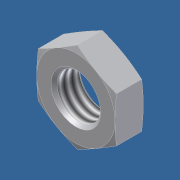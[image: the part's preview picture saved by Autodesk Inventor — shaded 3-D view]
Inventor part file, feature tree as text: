
AUTODESK INVENTOR PART (.ipt)
format: ipt  version: unknown  size: 220,160 bytes
history: native  units: in
note: dims shown in document units (in); Inventor stores cm internally (conversion verified against a paired STEP export)
features: other x70, sketch x3, revolve x2, extrude x1, thread x1
ambient origin geometry x8: Origin, YZ Plane, XZ Plane, XY Plane, X Axis, Y Axis, Z Axis, Center Point
feature tree (77):
  sketch  "Sketch_8"  dims[d0=360.0deg d1=0.25in d2=0.0in]
  sketch  "Sketch_10"  dims[d3=360.0deg d4=0.25in d5=0.0in]
  revolve  "Revolution1"  [1 undecoded]
  extrude  "Extrusion1"  Depth=0.25in TaperAngle=0.0deg
  revolve  "Revolution2"  [1 undecoded]
  thread  "Thread1"  [1 undecoded]
  other  "NUT_XY"
  other  "NUT_YZ"
  other  "NUT_ZX"
  other  "NUT_X"
  other  "NUT_Y"
  other  "NUT_Z"
  other  "NUT_Center"
  other  "a1_XY"
  other  "a1_YZ"
  other  "a1_ZX"
  other  "a1_X"
  other  "a1_Y"
  other  "a1_Z"
  other  "a1_Center"
  other  "a2_XY"
  other  "a2_YZ"
  other  "a2_ZX"
  other  "a2_X"
  other  "a2_Y"
  other  "a2_Z"
  other  "a2_Center"
  other  "b1_XY"
  other  "b1_YZ"
  other  "b1_ZX"
  other  "b1_X"
  other  "b1_Y"
  other  "b1_Z"
  other  "b1_Center"
  other  "b2_XY"
  other  "b2_YZ"
  other  "b2_ZX"
  other  "b2_X"
  other  "b2_Y"
  other  "b2_Z"
  other  "b2_Center"
  other  "e_XY"
  other  "e_YZ"
  other  "e_ZX"
  other  "e_X"
  other  "e_Y"
  other  "e_Z"
  other  "e_Center"
  other  "ol1_XY"
  other  "ol1_YZ"
  other  "ol1_ZX"
  other  "ol1_X"
  other  "ol1_Y"
  other  "ol1_Z"
  other  "ol1_Center"
  other  "ol2_XY"
  other  "ol2_YZ"
  other  "ol2_ZX"
  other  "ol2_X"
  other  "ol2_Y"
  other  "ol2_Z"
  other  "ol2_Center"
  other  "th1_XY"
  other  "th1_YZ"
  other  "th1_ZX"
  other  "th1_X"
  other  "th1_Y"
  other  "th1_Z"
  other  "th1_Center"
  other  "th2_XY"
  other  "th2_YZ"
  other  "th2_ZX"
  other  "th2_X"
  other  "th2_Y"
  other  "th2_Z"
  other  "th2_Center"
  sketch  "Sketch_11"
note: 3 required parameter values undecoded (feature->parameter linkage not recoverable at this tier; creation-order binding heuristic only, values carry confidence <= 0.55)